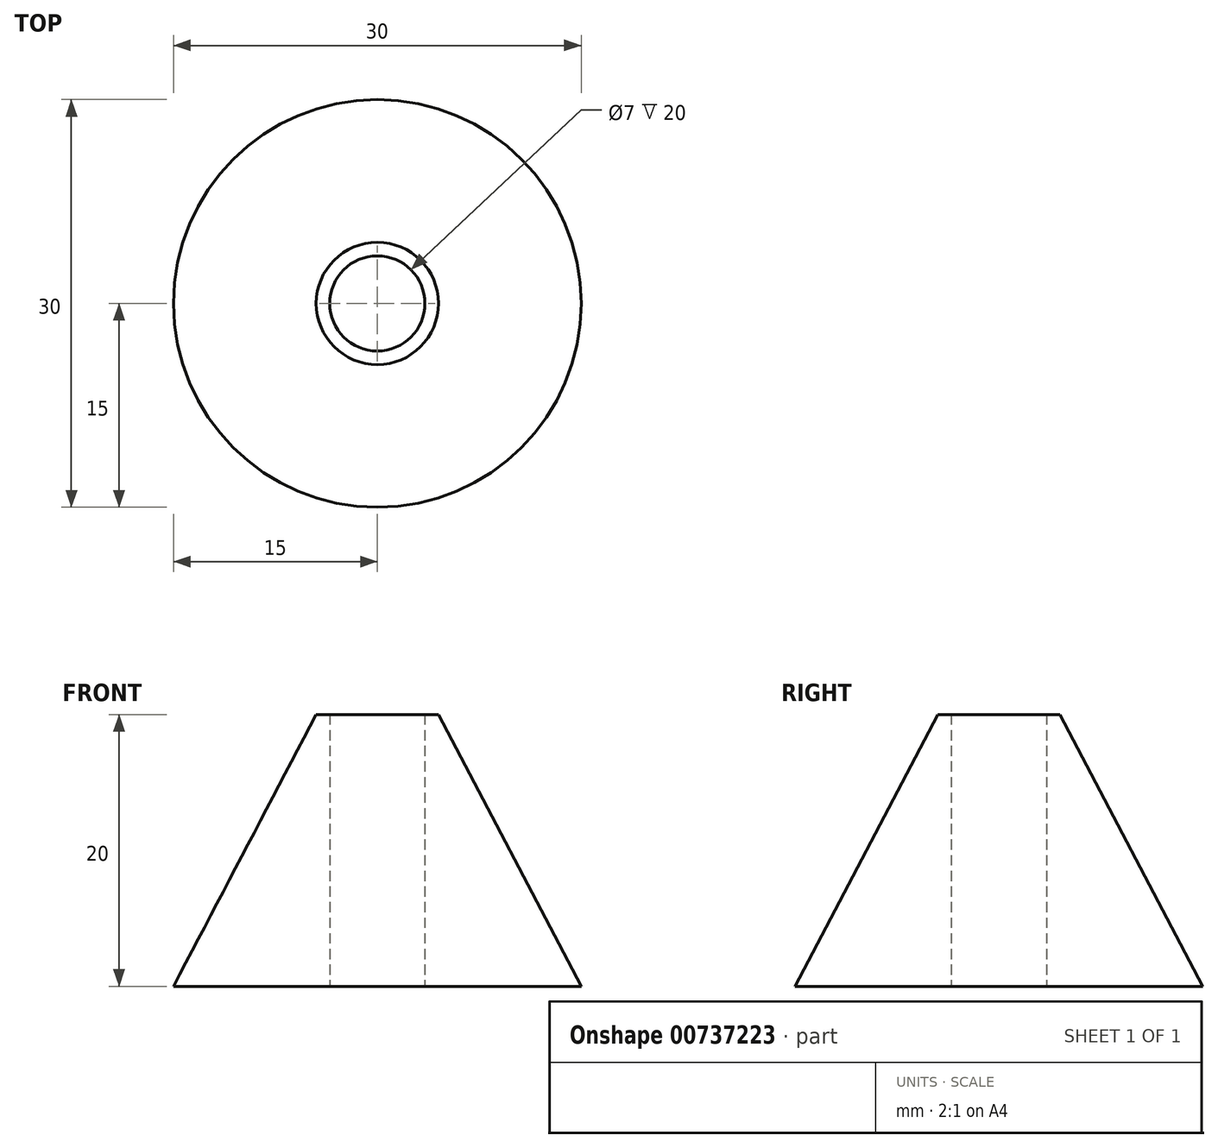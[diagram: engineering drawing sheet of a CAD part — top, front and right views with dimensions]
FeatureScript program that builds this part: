
annotation { "Feature Type Name" : "Feature", "Feature Type Description" : "" }
export const myFeature = defineFeature(function(context is Context, id is Id, definition is map)
    precondition{}
    {
        {
            var Q0;
            Q0=qCreatedBy(makeId("Front.planeOp"),FACE);
            var sketch = newSketch(context, id + "F0", { "sketchPlane" : qUnion([Q0])});
            skLineSegment(sketch, "E0", {"start": v(0, 0) * mm, "end": v(0, 11.2) * mm, "construction": true});
            skLineSegment(sketch, "E1", {"start": v(3.5, 0) * mm, "end": v(3.5, 20) * mm});
            skLineSegment(sketch, "E2", {"start": v(3.5, 20) * mm, "end": v(4.5, 20) * mm});
            skLineSegment(sketch, "E3", {"start": v(4.5, 20) * mm, "end": v(15, 0) * mm});
            skLineSegment(sketch, "E4", {"start": v(15, 0) * mm, "end": v(3.5, 0) * mm});
            skSolve(sketch);
        }
        {
            var Q0;
            Q0=makeQuery(id+"F0.imprint","IMPRINT",FACE,{"disambiguationData":[TD([[makeQuery(id+"F0.imprint","IMPRINT",EDGE,{"derivedFrom":sQuery(id+"F0.wireOp",EDGE,"E1")}),-1.0]])]});
            var Q1;
            Q1=sQuery(id+"F0.wireOp",EDGE,"E0");
            revolve(context, id + "F1", {"surfaceOperationType" : NewSurfaceOperationType.NEW, "entities" : qUnion([Q0]), "axis" : qUnion([Q1]), "revolveType" : RevolveType.FULL});
        }
    });
